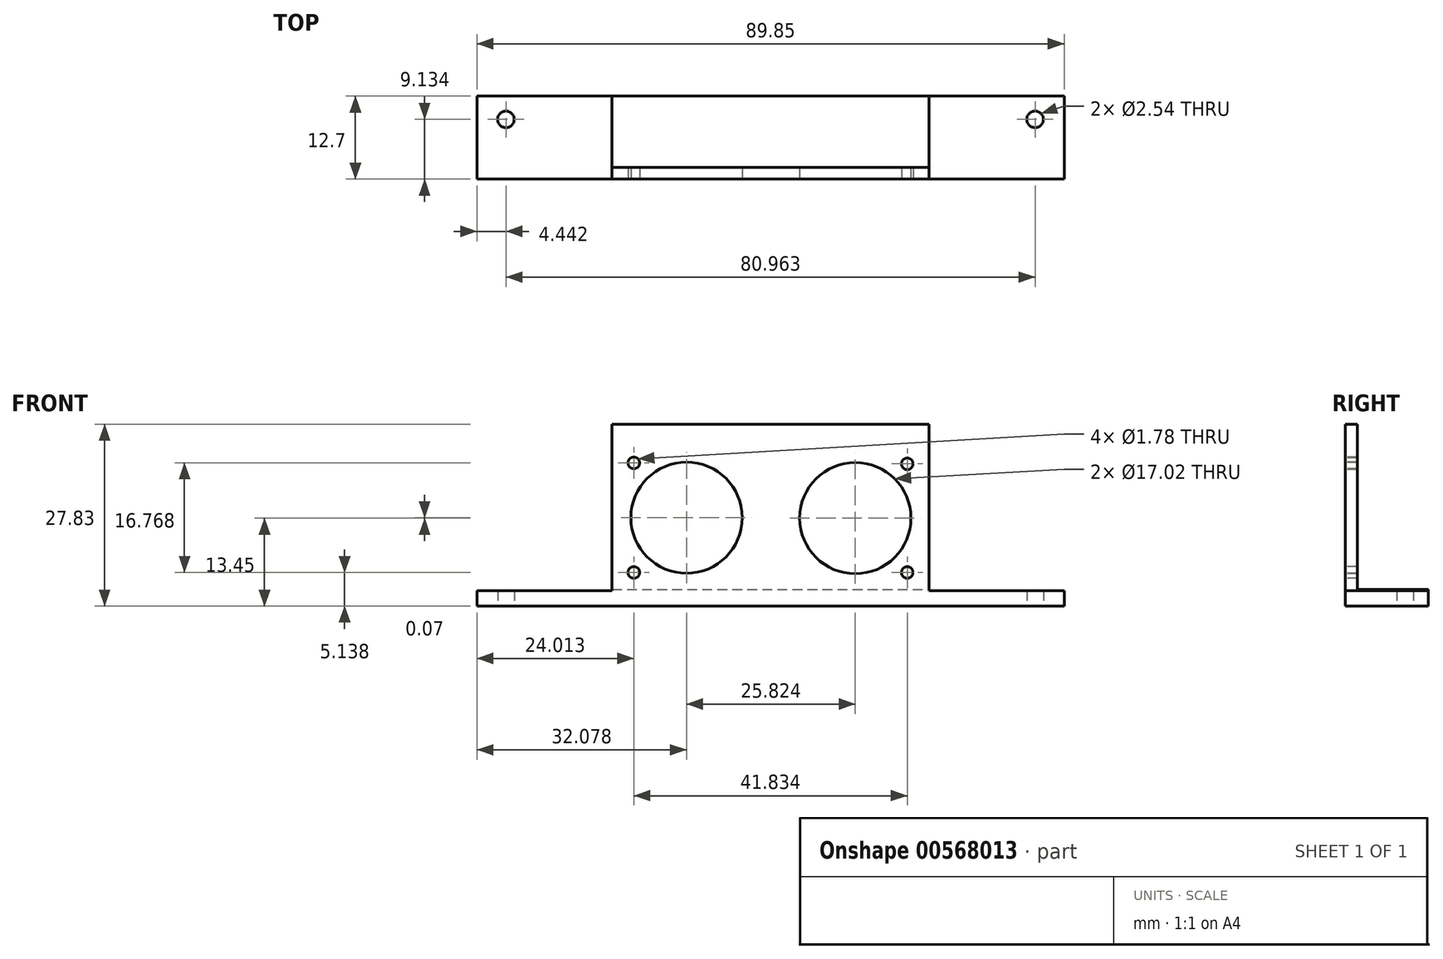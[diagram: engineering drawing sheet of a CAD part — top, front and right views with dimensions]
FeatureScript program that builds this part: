
annotation { "Feature Type Name" : "Feature", "Feature Type Description" : "" }
export const myFeature = defineFeature(function(context is Context, id is Id, definition is map)
    precondition{}
    {
        {
            var Q0;
            Q0=qCreatedBy(makeId("Top.planeOp"),FACE);
            var sketch = newSketch(context, id + "F0", { "sketchPlane" : qUnion([Q0])});
            skLineSegment(sketch, "E0.bottom", {"start": v(-42.93, -15.36) * mm, "end": v(46.92, -15.36) * mm});
            skLineSegment(sketch, "E0.top", {"start": v(-42.93, -28.06) * mm, "end": v(46.92, -28.06) * mm});
            skLineSegment(sketch, "E0.left", {"start": v(-42.93, -15.36) * mm, "end": v(-42.93, -28.06) * mm});
            skLineSegment(sketch, "E0.right", {"start": v(46.92, -15.36) * mm, "end": v(46.92, -28.06) * mm});
            skCircle(sketch, "E1", {"center": v(-38.49, -18.93) * mm, "radius": 1.27 * mm});
            skCircle(sketch, "E2", {"center": v(42.47, -18.93) * mm, "radius": 1.27 * mm});
            skLineSegment(sketch, "E3", {"start": v(-38.49, -18.93) * mm, "end": v(42.47, -18.93) * mm});
            skLineSegment(sketch, "E4", {"start": v(-38.49, -18.93) * mm, "end": v(-42.93, -18.93) * mm});
            skLineSegment(sketch, "E5", {"start": v(42.47, -18.93) * mm, "end": v(46.92, -18.93) * mm});
            skSolve(sketch);
        }
        {
            var Q0;
            Q0=makeQuery(id+"F0.imprint","IMPRINT",FACE,{"disambiguationData":[TD([[makeQuery(id+"F0.imprint","IMPRINT",EDGE,{"derivedFrom":sQuery(id+"F0.wireOp",EDGE,"E0.bottom")}),-1.0]])]});
            var Q1;
            {var subQ6=sQuery(id+"F0.wireOp",EDGE,"E0.top");Q1=makeQuery(id+"F0.imprint","IMPRINT",FACE,{"disambiguationData":[TD([[makeQuery(id+"F0.imprint","IMPRINT",EDGE,{"derivedFrom":subQ6}),1.0]])]});}
            extrude(context, id + "F1", {"entities" : qUnion([Q0, Q1]), "depth" : 2.54 * mm, "offsetDistance" : 25.4 * mm});
        }
        {
            var Q0;
            Q0=makeQuery(id+"F1.opExtrude","CAP_FACE",FACE,{"disambiguationData":[OSD([sQuery(id+"F0.wireOp",EDGE,"E0.bottom"),sQuery(id+"F0.wireOp",EDGE,"E0.top"),sQuery(id+"F0.wireOp",EDGE,"E0.left"),sQuery(id+"F0.wireOp",EDGE,"E0.right"),sQuery(id+"F0.wireOp",EDGE,"E1"),sQuery(id+"F0.wireOp",EDGE,"E2")])],"isStart":false});
            var sketch = newSketch(context, id + "F2", { "sketchPlane" : qUnion([Q0])});
            skLineSegment(sketch, "E6.bottom", {"start": v(-42.93, -26.27) * mm, "end": v(46.92, -26.27) * mm});
            skLineSegment(sketch, "E6.top", {"start": v(-42.93, -28.06) * mm, "end": v(46.92, -28.06) * mm});
            skLineSegment(sketch, "E6.left", {"start": v(-42.93, -26.27) * mm, "end": v(-42.93, -28.06) * mm});
            skLineSegment(sketch, "E6.right", {"start": v(46.92, -26.27) * mm, "end": v(46.92, -28.06) * mm});
            skSolve(sketch);
        }
        {
            var Q0;
            Q0=makeQuery(id+"F2.imprint","IMPRINT",FACE,{"disambiguationData":[TD([[makeQuery(id+"F2.imprint","IMPRINT",EDGE,{"derivedFrom":sQuery(id+"F2.wireOp",EDGE,"E6.bottom")}),-1.0]])]});
            extrude(context, id + "F3", {"entities" : qUnion([Q0]), "operationType" : NewBodyOperationType.ADD, "depth" : 50.8 * mm, "offsetDistance" : 25.4 * mm});
        }
        {
            var Q0;
            Q0=makeQuery(id+"F3.boolean.opBoolean","MERGE",FACE,{"derivedFrom":[makeQuery(id+"F1.opExtrude","SWEPT_FACE",FACE,{"disambiguationData":[OSD([sQuery(id+"F0.wireOp",EDGE,"E0.top")])]}),makeQuery(id+"F3.opExtrude","SWEPT_FACE",FACE,{"disambiguationData":[OSD([sQuery(id+"F2.wireOp",EDGE,"E6.top")])]})]});
            var sketch = newSketch(context, id + "F4", { "sketchPlane" : qUnion([Q0])});
            skCircle(sketch, "E7", {"center": v(-18.92, 21.9) * mm, "radius": 0.89 * mm});
            skCircle(sketch, "E8", {"center": v(22.92, 21.76) * mm, "radius": 0.89 * mm});
            skCircle(sketch, "E9", {"center": v(-18.92, 5.14) * mm, "radius": 0.89 * mm});
            skCircle(sketch, "E10", {"center": v(22.92, 5.14) * mm, "radius": 0.89 * mm});
            skCircle(sketch, "E11", {"center": v(-10.85, 13.52) * mm, "radius": 8.5 * mm});
            skCircle(sketch, "E12", {"center": v(14.97, 13.45) * mm, "radius": 8.5 * mm});
            skLineSegment(sketch, "E13.bottom", {"start": v(-42.93, 53.34) * mm, "end": v(-22.24, 53.34) * mm});
            skLineSegment(sketch, "E13.top", {"start": v(-42.93, 2.33) * mm, "end": v(-22.24, 2.33) * mm});
            skLineSegment(sketch, "E13.left", {"start": v(-42.93, 53.34) * mm, "end": v(-42.93, 2.33) * mm});
            skLineSegment(sketch, "E13.right", {"start": v(-22.24, 53.34) * mm, "end": v(-22.24, 2.33) * mm});
            skLineSegment(sketch, "E14.bottom", {"start": v(26.24, 2.33) * mm, "end": v(46.92, 2.33) * mm});
            skLineSegment(sketch, "E14.top", {"start": v(26.24, 53.34) * mm, "end": v(46.92, 53.34) * mm});
            skLineSegment(sketch, "E14.left", {"start": v(26.24, 2.33) * mm, "end": v(26.24, 53.34) * mm});
            skLineSegment(sketch, "E14.right", {"start": v(46.92, 2.33) * mm, "end": v(46.92, 53.34) * mm});
            skLineSegment(sketch, "E15", {"start": v(-22.24, 27.83) * mm, "end": v(26.24, 27.83) * mm});
            skSolve(sketch);
        }
        {
            var Q0;
            Q0=makeQuery(id+"F4.imprint","IMPRINT",FACE,{"disambiguationData":[TD([[makeQuery(id+"F4.imprint","IMPRINT",EDGE,{"derivedFrom":sQuery(id+"F4.wireOp",EDGE,"E11")}),1.0]])]});
            var Q1;
            Q1=makeQuery(id+"F4.imprint","IMPRINT",FACE,{"disambiguationData":[TD([[makeQuery(id+"F4.imprint","IMPRINT",EDGE,{"derivedFrom":sQuery(id+"F4.wireOp",EDGE,"E12")}),1.0]])]});
            var Q2;
            Q2=makeQuery(id+"F4.imprint","IMPRINT",FACE,{"disambiguationData":[TD([[makeQuery(id+"F4.imprint","IMPRINT",EDGE,{"derivedFrom":sQuery(id+"F4.wireOp",EDGE,"E7")}),1.0]])]});
            var Q3;
            Q3=makeQuery(id+"F4.imprint","IMPRINT",FACE,{"disambiguationData":[TD([[makeQuery(id+"F4.imprint","IMPRINT",EDGE,{"derivedFrom":sQuery(id+"F4.wireOp",EDGE,"E9")}),1.0]])]});
            var Q4;
            Q4=makeQuery(id+"F4.imprint","IMPRINT",FACE,{"disambiguationData":[TD([[makeQuery(id+"F4.imprint","IMPRINT",EDGE,{"derivedFrom":sQuery(id+"F4.wireOp",EDGE,"E10")}),1.0]])]});
            var Q5;
            Q5=makeQuery(id+"F4.imprint","IMPRINT",FACE,{"disambiguationData":[TD([[makeQuery(id+"F4.imprint","IMPRINT",EDGE,{"derivedFrom":sQuery(id+"F4.wireOp",EDGE,"E8")}),1.0]])]});
            var Q6;
            Q6=makeQuery(id+"F4.imprint","IMPRINT",FACE,{"disambiguationData":[TD([[makeQuery(id+"F4.imprint","IMPRINT",EDGE,{"derivedFrom":sQuery(id+"F4.wireOp",EDGE,"cPAGVTbV-xUEE-PMVC-DcMK-ZMClatmGxtQl.bottom")}),-1.0]])]});
            var Q7;
            Q7=makeQuery(id+"F4.imprint","IMPRINT",FACE,{"disambiguationData":[TD([[makeQuery(id+"F4.imprint","IMPRINT",EDGE,{"derivedFrom":sQuery(id+"F4.wireOp",EDGE,"apBiRRL4-24SH-TikN-sm67-61VB3tnNHCzQ.bottom")}),-1.0]])]});
            var Q8;
            Q8=makeQuery(id+"F4.imprint","IMPRINT",FACE,{"disambiguationData":[TD([[makeQuery(id+"F4.imprint","IMPRINT",EDGE,{"derivedFrom":sQuery(id+"F4.wireOp",EDGE,"vxKcHli7-F613-Z7T3-PYHH-ROlf1OeppP6P.bottom")}),1.0]])]});
            var Q9;
            {var subQ0=sQuery(id+"F4.wireOp",EDGE,"cPAGVTbV-xUEE-PMVC-DcMK-ZMClatmGxtQl.right");var subQ1=sQuery(id+"F4.wireOp",EDGE,"cPAGVTbV-xUEE-PMVC-DcMK-ZMClatmGxtQl.top");var subQ2=makeQuery(id+"F4.imprint","INTERSECT",VERTEX,{"derivedFrom":[subQ1,subQ0]});Q9=makeQuery(id+"F4.imprint","IMPRINT",FACE,{"disambiguationData":[TD([[makeQuery(id+"F4.imprint","IMPRINT",EDGE,{"disambiguationData":[TD([[subQ2,1.0]])],"derivedFrom":subQ1}),1.0]])]});}
            var Q10;
            {var subQ0=sQuery(id+"F4.wireOp",EDGE,"cPAGVTbV-xUEE-PMVC-DcMK-ZMClatmGxtQl.left");var subQ1=sQuery(id+"F4.wireOp",EDGE,"cPAGVTbV-xUEE-PMVC-DcMK-ZMClatmGxtQl.top");var subQ2=makeQuery(id+"F4.imprint","INTERSECT",VERTEX,{"derivedFrom":[subQ1,subQ0]});Q10=makeQuery(id+"F4.imprint","IMPRINT",FACE,{"disambiguationData":[TD([[makeQuery(id+"F4.imprint","IMPRINT",EDGE,{"disambiguationData":[TD([[subQ2,-1.0]])],"derivedFrom":subQ1}),1.0]])]});}
            var Q11;
            Q11=makeQuery(id+"F4.imprint","IMPRINT",FACE,{"disambiguationData":[TD([[makeQuery(id+"F4.imprint","IMPRINT",EDGE,{"derivedFrom":sQuery(id+"F4.wireOp",EDGE,"E14.bottom")}),1.0]])]});
            var Q12;
            Q12=makeQuery(id+"F4.imprint","IMPRINT",FACE,{"disambiguationData":[TD([[makeQuery(id+"F4.imprint","IMPRINT",EDGE,{"derivedFrom":sQuery(id+"F4.wireOp",EDGE,"E13.bottom")}),-1.0]])]});
            var Q13;
            {var subQ3=sQuery(id+"F4.wireOp",EDGE,"E15");Q13=makeQuery(id+"F4.imprint","IMPRINT",FACE,{"disambiguationData":[TD([[makeQuery(id+"F4.imprint","IMPRINT",EDGE,{"derivedFrom":subQ3}),1.0]])]});}
            extrude(context, id + "F5", {"entities" : qUnion([Q0, Q1, Q2, Q3, Q4, Q5, Q6, Q7, Q8, Q9, Q10, Q11, Q12, Q13]), "operationType" : NewBodyOperationType.REMOVE, "oppositeDirection" : true, "depth" : 25.4 * mm, "offsetDistance" : 25.4 * mm});
        }
    });
